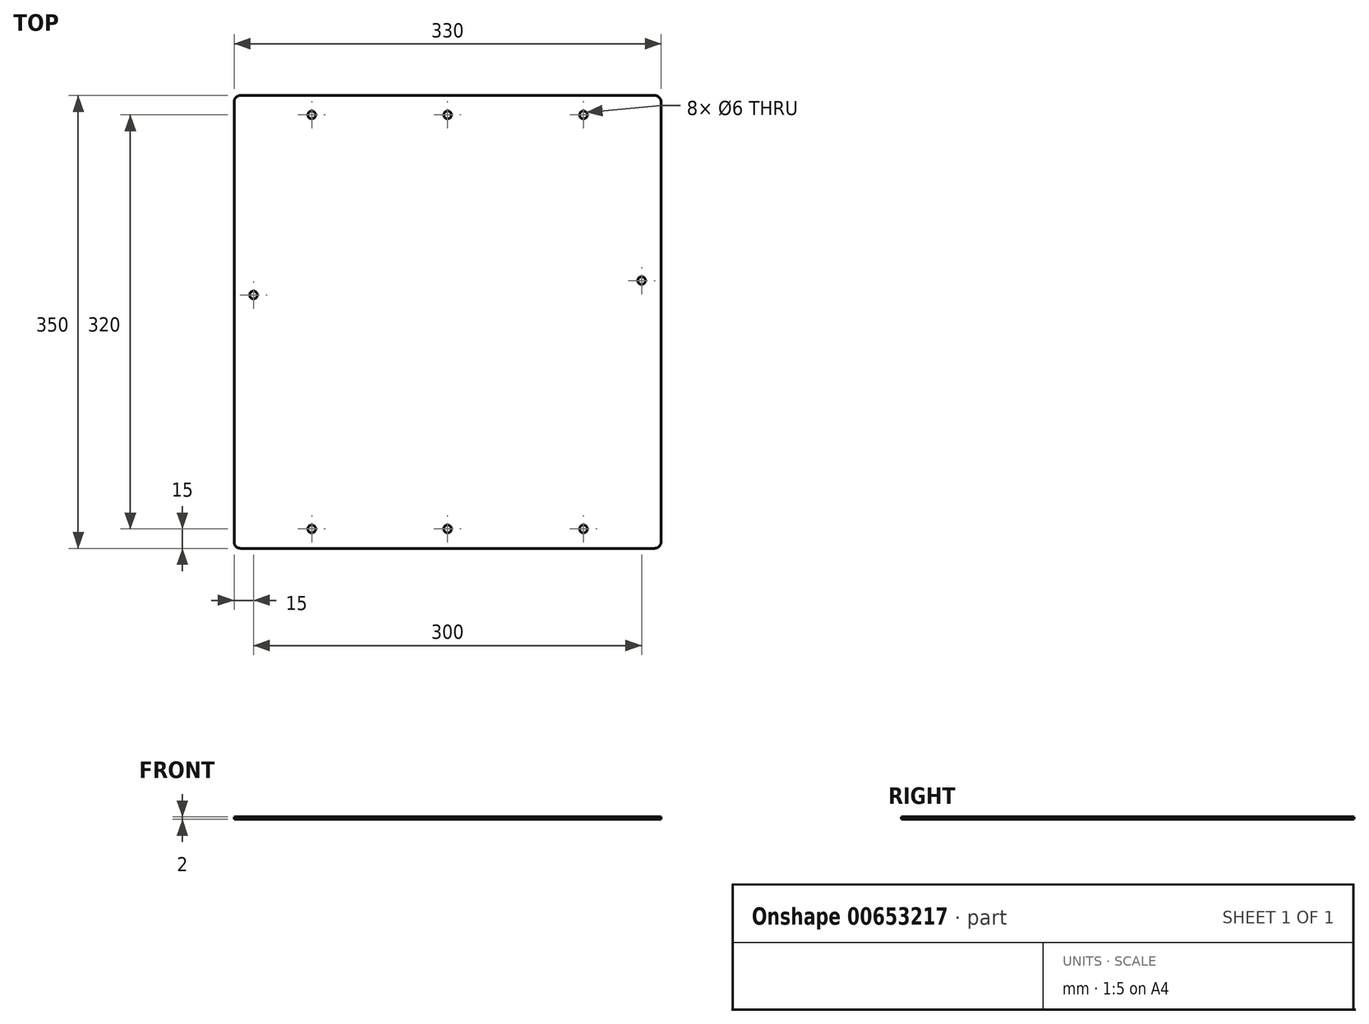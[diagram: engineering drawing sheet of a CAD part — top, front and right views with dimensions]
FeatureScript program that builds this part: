
annotation { "Feature Type Name" : "Feature", "Feature Type Description" : "" }
export const myFeature = defineFeature(function(context is Context, id is Id, definition is map)
    precondition{}
    {
        {
            var Q0;
            Q0=qCreatedBy(makeId("Top.planeOp"),FACE);
            var sketch = newSketch(context, id + "F0", { "sketchPlane" : qUnion([Q0])});
            skLineSegment(sketch, "E0.bottom", {"start": v(5, 0) * mm, "end": v(325, 0) * mm});
            skLineSegment(sketch, "E0.top", {"start": v(5, 350) * mm, "end": v(325, 350) * mm});
            skLineSegment(sketch, "E0.left", {"start": v(0, 5) * mm, "end": v(0, 345) * mm});
            skLineSegment(sketch, "E0.right", {"start": v(330, 5) * mm, "end": v(330, 345) * mm});
            skPoint(sketch, "E1.visualSharp", {"position": v(0, 350) * mm});
            skArc(sketch, "E1.filletArc", {"start": v(5, 350) * mm, "mid": v(1.46, 348.54) * mm, "end": v(0, 345) * mm});
            skPoint(sketch, "E2.visualSharp", {"position": v(330, 350) * mm});
            skArc(sketch, "E2.filletArc", {"start": v(330, 345) * mm, "mid": v(328.54, 348.54) * mm, "end": v(325, 350) * mm});
            skPoint(sketch, "E3.visualSharp", {"position": v(330, 0) * mm});
            skArc(sketch, "E3.filletArc", {"start": v(325, 0) * mm, "mid": v(328.54, 1.46) * mm, "end": v(330, 5) * mm});
            skPoint(sketch, "E4.visualSharp", {"position": v(0, 0) * mm});
            skArc(sketch, "E4.filletArc", {"start": v(0, 5) * mm, "mid": v(1.46, 1.46) * mm, "end": v(5, 0) * mm});
            skCircle(sketch, "E5", {"center": v(60, 15) * mm, "radius": 3 * mm});
            skCircle(sketch, "E6", {"center": v(165, 15) * mm, "radius": 3 * mm});
            skCircle(sketch, "E7", {"center": v(270, 15) * mm, "radius": 3 * mm});
            skCircle(sketch, "E8", {"center": v(60, 335) * mm, "radius": 3 * mm});
            skCircle(sketch, "E9", {"center": v(165, 335) * mm, "radius": 3 * mm});
            skCircle(sketch, "E10", {"center": v(270, 335) * mm, "radius": 3 * mm});
            skCircle(sketch, "E11", {"center": v(15, 195.84) * mm, "radius": 3 * mm});
            skCircle(sketch, "E12", {"center": v(315, 206.96) * mm, "radius": 3 * mm});
            skSolve(sketch);
        }
        {
            var Q0;
            Q0=makeQuery(id+"F0.imprint","IMPRINT",FACE,{"disambiguationData":[TD([[makeQuery(id+"F0.imprint","IMPRINT",EDGE,{"derivedFrom":sQuery(id+"F0.wireOp",EDGE,"E0.bottom")}),1.0]])]});
            extrude(context, id + "F1", {"entities" : qUnion([Q0]), "depth" : 2 * mm, "offsetDistance" : 25 * mm});
        }
    });
